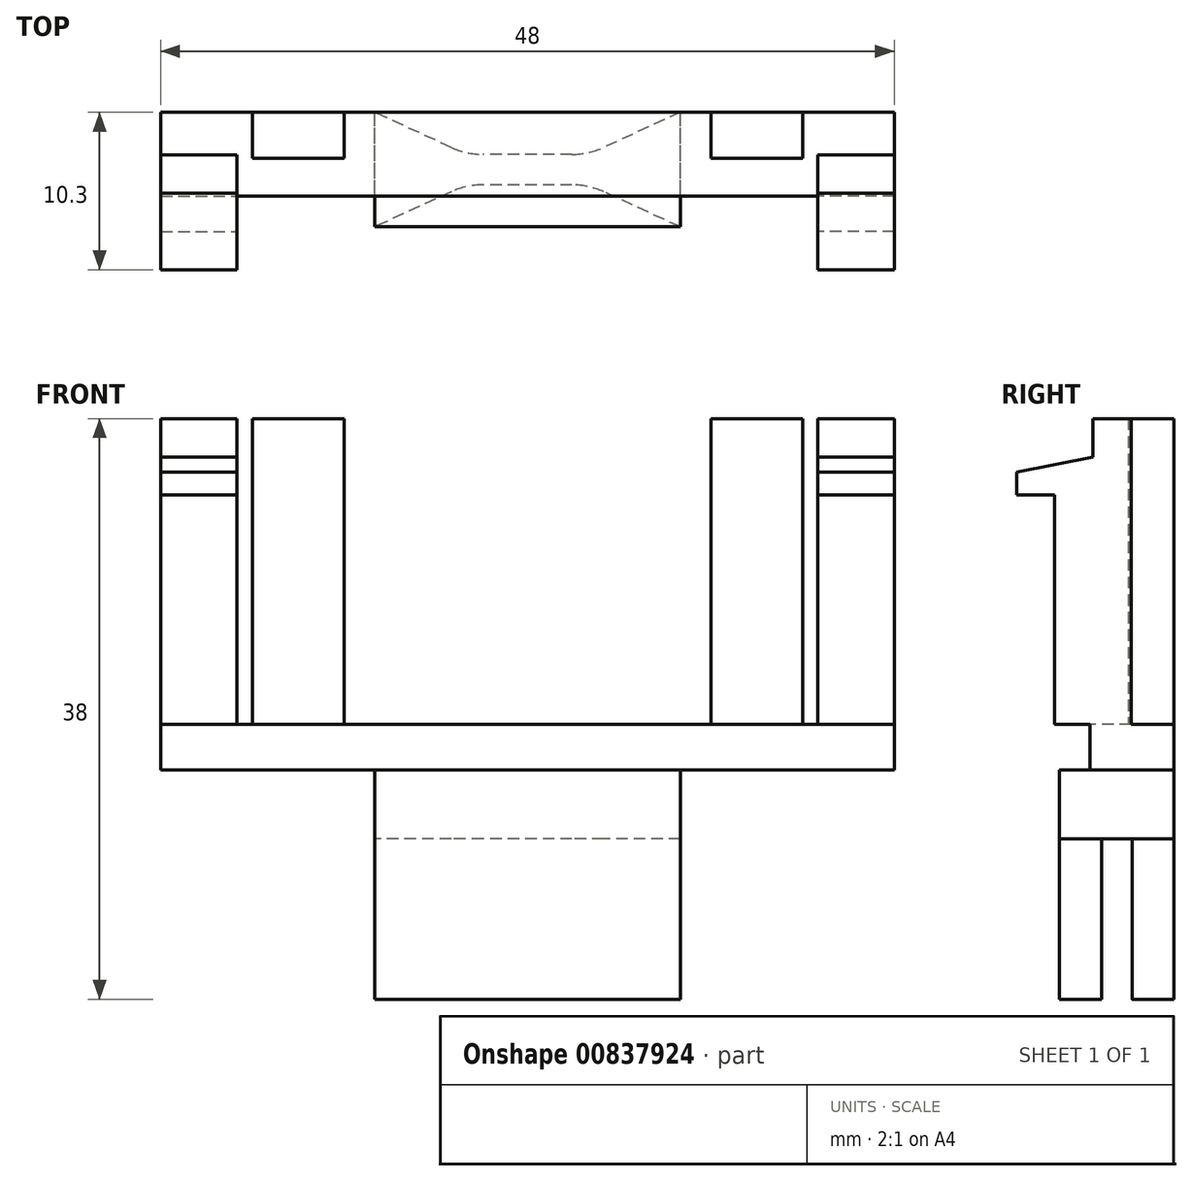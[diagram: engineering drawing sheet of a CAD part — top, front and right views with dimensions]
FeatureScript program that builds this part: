
annotation { "Feature Type Name" : "Feature", "Feature Type Description" : "" }
export const myFeature = defineFeature(function(context is Context, id is Id, definition is map)
    precondition{}
    {
        {
            var Q0;
            Q0=qCreatedBy(makeId("Top.planeOp"),FACE);
            var sketch = newSketch(context, id + "F0", { "sketchPlane" : qUnion([Q0])});
            skLineSegment(sketch, "E0.left", {"start": v(24, -2.75) * mm, "end": v(24, 2.75) * mm});
            skPoint(sketch, "E0.middle", {"position": v(0, 0) * mm});
            skLineSegment(sketch, "E1.bottom", {"start": v(-10, -4.75) * mm, "end": v(10, -4.75) * mm});
            skLineSegment(sketch, "E1.top", {"start": v(-10, 2.75) * mm, "end": v(10, 2.75) * mm});
            skLineSegment(sketch, "E1.left", {"start": v(-10, -4.75) * mm, "end": v(-10, 2.75) * mm});
            skLineSegment(sketch, "E1.right", {"start": v(10, -4.75) * mm, "end": v(10, 2.75) * mm});
            skLineSegment(sketch, "E2", {"start": v(0, -4.75) * mm, "end": v(0, 0) * mm});
            skLineSegment(sketch, "E3", {"start": v(24, 2.75) * mm, "end": v(10, 2.75) * mm});
            skLineSegment(sketch, "E4", {"start": v(24, -2.75) * mm, "end": v(10, -2.75) * mm});
            skLineSegment(sketch, "E5", {"start": v(10, -2.75) * mm, "end": v(-10, -2.75) * mm});
            skSolve(sketch);
        }
        {
            var Q0;
            Q0=makeQuery(id+"F0.imprint","IMPRINT",FACE,{"disambiguationData":[TD([[makeQuery(id+"F0.imprint","IMPRINT",EDGE,{"derivedFrom":sQuery(id+"F0.wireOp",EDGE,"E0.bottom")}),-1.0]])]});
            var Q1;
            {var subQ0=sQuery(id+"F0.wireOp",EDGE,"E0.right");Q1=makeQuery(id+"F0.imprint","IMPRINT",FACE,{"disambiguationData":[TD([[makeQuery(id+"F0.imprint","IMPRINT",EDGE,{"derivedFrom":subQ0}),-1.0]])]});}
            var Q2;
            {var subQ0=sQuery(id+"F0.wireOp",EDGE,"E0.left");Q2=makeQuery(id+"F0.imprint","IMPRINT",FACE,{"disambiguationData":[TD([[makeQuery(id+"F0.imprint","IMPRINT",EDGE,{"derivedFrom":subQ0}),1.0]])]});}
            var Q3;
            {var subQ1=sQuery(id+"F0.wireOp",EDGE,"E1.top");Q3=makeQuery(id+"F0.imprint","IMPRINT",FACE,{"disambiguationData":[TD([[makeQuery(id+"F0.imprint","IMPRINT",EDGE,{"derivedFrom":subQ1}),-1.0]])]});}
            extrude(context, id + "F1", {"entities" : qUnion([Q0, Q1, Q2, Q3]), "depth" : 3 * mm, "offsetDistance" : 25 * mm});
        }
        {
            var Q0;
            {var subQ0=sQuery(id+"F0.wireOp",EDGE,"E2");var subQ1=sQuery(id+"F0.wireOp",EDGE,"E0.bottom");var subQ2=makeQuery(id+"F0.imprint","INTERSECT",VERTEX,{"derivedFrom":[subQ1,subQ0]});Q0=makeQuery(id+"F0.imprint","IMPRINT",FACE,{"disambiguationData":[TD([[makeQuery(id+"F0.imprint","IMPRINT",EDGE,{"disambiguationData":[TD([[subQ2,-1.0]])],"derivedFrom":subQ1}),1.0]])]});}
            var Q1;
            {var subQ0=sQuery(id+"F0.wireOp",EDGE,"E1.right");var subQ1=sQuery(id+"F0.wireOp",EDGE,"E0.bottom");var subQ2=makeQuery(id+"F0.imprint","INTERSECT",VERTEX,{"derivedFrom":[subQ1,subQ0]});Q1=makeQuery(id+"F0.imprint","IMPRINT",FACE,{"disambiguationData":[TD([[makeQuery(id+"F0.imprint","IMPRINT",EDGE,{"disambiguationData":[TD([[subQ2,-1.0]])],"derivedFrom":subQ1}),1.0]])]});}
            var Q2;
            {var subQ0=sQuery(id+"F0.wireOp",EDGE,"E1.top");Q2=makeQuery(id+"F0.imprint","IMPRINT",FACE,{"disambiguationData":[TD([[makeQuery(id+"F0.imprint","IMPRINT",EDGE,{"derivedFrom":subQ0}),-1.0]])]});}
            var Q3;
            {var subQ0=sQuery(id+"F0.wireOp",EDGE,"E1.left");var subQ1=sQuery(id+"F0.wireOp",EDGE,"E1.bottom");var subQ2=makeQuery(id+"F0.imprint","INTERSECT",VERTEX,{"derivedFrom":[subQ1,subQ0]});Q3=makeQuery(id+"F0.imprint","IMPRINT",FACE,{"disambiguationData":[TD([[makeQuery(id+"F0.imprint","IMPRINT",EDGE,{"disambiguationData":[TD([[subQ2,-1.0]])],"derivedFrom":subQ1}),1.0]])]});}
            var Q4;
            {var subQ0=sQuery(id+"F0.wireOp",EDGE,"E1.right");var subQ1=sQuery(id+"F0.wireOp",EDGE,"E1.bottom");var subQ2=makeQuery(id+"F0.imprint","INTERSECT",VERTEX,{"derivedFrom":[subQ1,subQ0]});Q4=makeQuery(id+"F0.imprint","IMPRINT",FACE,{"disambiguationData":[TD([[makeQuery(id+"F0.imprint","IMPRINT",EDGE,{"disambiguationData":[TD([[subQ2,1.0]])],"derivedFrom":subQ1}),1.0]])]});}
            var Q5;
            Q5=sQuery(id+"F0.wireOp",EDGE,"E1.bottom");
            extrude(context, id + "F2", {"entities" : qUnion([Q0, Q1, Q2, Q3, Q4]), "operationType" : NewBodyOperationType.ADD, "surfaceEntities" : qUnion([Q5]), "oppositeDirection" : true, "depth" : 4.5 * mm, "offsetDistance" : 25 * mm});
        }
        {
            var Q0;
            Q0=makeQuery(id+"F2.opExtrude","CAP_FACE",FACE,{"disambiguationData":[OSD([sQuery(id+"F0.wireOp",EDGE,"E1.bottom"),sQuery(id+"F0.wireOp",EDGE,"E1.top"),sQuery(id+"F0.wireOp",EDGE,"E1.left"),sQuery(id+"F0.wireOp",EDGE,"E1.right")])],"isStart":false});
            var sketch = newSketch(context, id + "F3", { "sketchPlane" : qUnion([Q0])});
            skLineSegment(sketch, "E6", {"start": v(10, -2.75) * mm, "end": v(4, 0) * mm});
            skLineSegment(sketch, "E7", {"start": v(4, 0) * mm, "end": v(-4, 0) * mm});
            skLineSegment(sketch, "E8", {"start": v(-4, 0) * mm, "end": v(-10, -2.75) * mm});
            skLineSegment(sketch, "E9", {"start": v(0, -2.75) * mm, "end": v(0, 4.75) * mm});
            skLineSegment(sketch, "E10", {"start": v(10, 1) * mm, "end": v(-10, 1) * mm});
            skLineSegment(sketch, "E11.MirrorCS", {"start": v(10, 4.75) * mm, "end": v(4, 2) * mm});
            skLineSegment(sketch, "E12.MirrorCS", {"start": v(4, 2) * mm, "end": v(-4, 2) * mm});
            skLineSegment(sketch, "E13.MirrorCS", {"start": v(-4, 2) * mm, "end": v(-10, 4.75) * mm});
            skSolve(sketch);
        }
        {
            var Q0;
            {var subQ0=sQuery(id+"F3.wireOp",EDGE,"E6");Q0=makeQuery(id+"F3.imprint","IMPRINT",FACE,{"disambiguationData":[TD([[makeQuery(id+"F3.imprint","IMPRINT",EDGE,{"derivedFrom":subQ0}),1.0]])]});}
            var Q1;
            {var subQ0=sQuery(id+"F3.wireOp",EDGE,"E8");Q1=makeQuery(id+"F3.imprint","IMPRINT",FACE,{"disambiguationData":[TD([[makeQuery(id+"F3.imprint","IMPRINT",EDGE,{"derivedFrom":subQ0}),1.0]])]});}
            var Q2;
            {var subQ5=sQuery(id+"F3.wireOp",EDGE,"E11.MirrorCS");Q2=makeQuery(id+"F3.imprint","IMPRINT",FACE,{"disambiguationData":[TD([[makeQuery(id+"F3.imprint","IMPRINT",EDGE,{"derivedFrom":subQ5}),-1.0]])]});}
            var Q3;
            {var subQ5=sQuery(id+"F3.wireOp",EDGE,"E13.MirrorCS");Q3=makeQuery(id+"F3.imprint","IMPRINT",FACE,{"disambiguationData":[TD([[makeQuery(id+"F3.imprint","IMPRINT",EDGE,{"derivedFrom":subQ5}),-1.0]])]});}
            extrude(context, id + "F4", {"entities" : qUnion([Q0, Q1, Q2, Q3]), "operationType" : NewBodyOperationType.ADD, "depth" : 10.5 * mm, "offsetDistance" : 25 * mm});
        }
        {
            var Q0;
            Q0=makeQuery(id+"F1.opExtrude","CAP_FACE",FACE,{"disambiguationData":[OSD([sQuery(id+"F0.wireOp",EDGE,"E0.bottom"),sQuery(id+"F0.wireOp",EDGE,"E0.top"),sQuery(id+"F0.wireOp",EDGE,"E0.left"),sQuery(id+"F0.wireOp",EDGE,"E0.right"),sQuery(id+"F0.wireOp",EDGE,"E1.top")])],"isStart":false});
            var sketch = newSketch(context, id + "F5", { "sketchPlane" : qUnion([Q0])});
            skLineSegment(sketch, "E14.bottom", {"start": v(12, 2.75) * mm, "end": v(18, 2.75) * mm});
            skLineSegment(sketch, "E14.top", {"start": v(12, -0.25) * mm, "end": v(18, -0.25) * mm});
            skLineSegment(sketch, "E14.left", {"start": v(12, 2.75) * mm, "end": v(12, -0.25) * mm});
            skLineSegment(sketch, "E14.right", {"start": v(18, 2.75) * mm, "end": v(18, -0.25) * mm});
            skLineSegment(sketch, "E15.bottom", {"start": v(24, -0.05) * mm, "end": v(19, -0.05) * mm});
            skLineSegment(sketch, "E15.top", {"start": v(24, -5.05) * mm, "end": v(19, -5.05) * mm});
            skLineSegment(sketch, "E15.left", {"start": v(24, -0.05) * mm, "end": v(24, -5.05) * mm});
            skLineSegment(sketch, "E15.right", {"start": v(19, -0.05) * mm, "end": v(19, -5.05) * mm});
            skSolve(sketch);
        }
        {
            var Q0;
            Q0=makeQuery(id+"F5.imprint","IMPRINT",FACE,{"disambiguationData":[TD([[makeQuery(id+"F5.imprint","IMPRINT",EDGE,{"derivedFrom":sQuery(id+"F5.wireOp",EDGE,"E14.bottom")}),-1.0]])]});
            var Q1;
            {var subQ0=sQuery(id+"F5.wireOp",EDGE,"E15.bottom");Q1=makeQuery(id+"F5.imprint","IMPRINT",FACE,{"disambiguationData":[TD([[makeQuery(id+"F5.imprint","IMPRINT",EDGE,{"derivedFrom":subQ0}),1.0]])]});}
            var Q2;
            {var subQ0=sQuery(id+"F5.wireOp",EDGE,"E15.top");Q2=makeQuery(id+"F5.imprint","IMPRINT",FACE,{"disambiguationData":[TD([[makeQuery(id+"F5.imprint","IMPRINT",EDGE,{"derivedFrom":subQ0}),-1.0]])]});}
            var Q3;
            Q3=makeQuery(id+"F5.imprint","IMPRINT",FACE,{"disambiguationData":[TD([[makeQuery(id+"F5.imprint","IMPRINT",EDGE,{"derivedFrom":sQuery(id+"F5.wireOp",EDGE,"5ea3a386-2e72-4d6f-82df-83e3c4ea288f0.MirrorCS")}),-1.0]])]});
            var Q4;
            {var subQ0=sQuery(id+"F5.wireOp",EDGE,"6e2690fa-45c8-4787-880a-55a10225b8a60.MirrorCS");Q4=makeQuery(id+"F5.imprint","IMPRINT",FACE,{"disambiguationData":[TD([[makeQuery(id+"F5.imprint","IMPRINT",EDGE,{"derivedFrom":subQ0}),-1.0]])]});}
            var Q5;
            {var subQ0=sQuery(id+"F5.wireOp",EDGE,"0a7195a1-aad8-4bab-bf7f-33c16b91a9020.MirrorCS");Q5=makeQuery(id+"F5.imprint","IMPRINT",FACE,{"disambiguationData":[TD([[makeQuery(id+"F5.imprint","IMPRINT",EDGE,{"derivedFrom":subQ0}),1.0]])]});}
            var Q6;
            Q6=makeQuery(id+"F5.imprint","IMPRINT",FACE,{"disambiguationData":[TD([[makeQuery(id+"F5.imprint","IMPRINT",EDGE,{"derivedFrom":sQuery(id+"F5.wireOp",EDGE,"E14.bottom")}),1.0]])]});
            extrude(context, id + "F6", {"entities" : qUnion([Q0, Q1, Q2, Q3, Q4, Q5, Q6]), "operationType" : NewBodyOperationType.ADD, "depth" : 15 * mm, "offsetDistance" : 25 * mm});
        }
        {
            var Q0;
            Q0=makeQuery(id+"F6.opExtrude","CAP_FACE",FACE,{"disambiguationData":[OSD([sQuery(id+"F5.wireOp",EDGE,"E15.bottom"),sQuery(id+"F5.wireOp",EDGE,"E15.top"),sQuery(id+"F5.wireOp",EDGE,"E15.left"),sQuery(id+"F5.wireOp",EDGE,"E15.right")])],"isStart":false});
            var sketch = newSketch(context, id + "F7", { "sketchPlane" : qUnion([Q0])});
            skLineSegment(sketch, "E16.bottom", {"start": v(19, -0.05) * mm, "end": v(24, -0.05) * mm});
            skLineSegment(sketch, "E16.top", {"start": v(19, -2.55) * mm, "end": v(24, -2.55) * mm});
            skLineSegment(sketch, "E16.left", {"start": v(19, -0.05) * mm, "end": v(19, -2.55) * mm});
            skLineSegment(sketch, "E16.right", {"start": v(24, -0.05) * mm, "end": v(24, -2.55) * mm});
            skSolve(sketch);
        }
        {
            var Q0;
            Q0=makeQuery(id+"F7.imprint","IMPRINT",FACE,{"disambiguationData":[TD([[makeQuery(id+"F7.imprint","IMPRINT",EDGE,{"derivedFrom":sQuery(id+"F7.wireOp",EDGE,"e6cad59b-8b4a-41b5-838e-72c1b71bfee10.MirrorCS")}),1.0]])]});
            var Q1;
            Q1=makeQuery(id+"F6.opExtrude","CAP_FACE",FACE,{"disambiguationData":[OSD([sQuery(id+"F5.wireOp",EDGE,"5ea3a386-2e72-4d6f-82df-83e3c4ea288f0.MirrorCS"),sQuery(id+"F5.wireOp",EDGE,"cba0519a-8970-4dc6-bb50-976fce54e4630.MirrorCS"),sQuery(id+"F5.wireOp",EDGE,"64ce6bfb-654b-4831-a077-69f9ca763c0d0.MirrorCS"),sQuery(id+"F5.wireOp",EDGE,"2814ab19-4fc1-4c3a-880c-0dd651a3744e0.MirrorCS")])],"isStart":false});
            var Q2;
            Q2=makeQuery(id+"F6.opExtrude","CAP_FACE",FACE,{"disambiguationData":[OSD([sQuery(id+"F5.wireOp",EDGE,"E14.bottom"),sQuery(id+"F5.wireOp",EDGE,"E14.top"),sQuery(id+"F5.wireOp",EDGE,"E14.left"),sQuery(id+"F5.wireOp",EDGE,"E14.right")])],"isStart":false});
            var Q3;
            Q3=makeQuery(id+"F7.imprint","IMPRINT",FACE,{"disambiguationData":[TD([[makeQuery(id+"F7.imprint","IMPRINT",EDGE,{"derivedFrom":sQuery(id+"F7.wireOp",EDGE,"E16.bottom")}),1.0]])]});
            extrude(context, id + "F8", {"entities" : qUnion([Q0, Q1, Q2, Q3]), "operationType" : NewBodyOperationType.ADD, "depth" : 5 * mm, "offsetDistance" : 25 * mm});
        }
        {
            var Q0;
            Q0=makeQuery(id+"F8.boolean.opBoolean","MERGE",FACE,{"derivedFrom":[makeQuery(id+"F6.boolean.opBoolean","MERGE",FACE,{"derivedFrom":[makeQuery(id+"F1.opExtrude","SWEPT_FACE",FACE,{"disambiguationData":[OSD([sQuery(id+"F0.wireOp",EDGE,"E0.left")])]}),makeQuery(id+"F6.opExtrude","SWEPT_FACE",FACE,{"disambiguationData":[OSD([sQuery(id+"F5.wireOp",EDGE,"E15.left")])]})]}),makeQuery(id+"F8.opExtrude","SWEPT_FACE",FACE,{"disambiguationData":[OSD([sQuery(id+"F7.wireOp",EDGE,"E16.right")])]})]});
            var sketch = newSketch(context, id + "F9", { "sketchPlane" : qUnion([Q0])});
            skLineSegment(sketch, "E17.bottom", {"start": v(-2.55, 18) * mm, "end": v(-7.55, 18) * mm});
            skLineSegment(sketch, "E17.top", {"start": v(-2.55, 19.5) * mm, "end": v(-7.55, 19.5) * mm});
            skLineSegment(sketch, "E17.left", {"start": v(-2.55, 18) * mm, "end": v(-2.55, 19.5) * mm});
            skLineSegment(sketch, "E17.right", {"start": v(-7.55, 18) * mm, "end": v(-7.55, 19.5) * mm});
            skLineSegment(sketch, "E18", {"start": v(-7.55, 19.5) * mm, "end": v(-2.55, 20.5) * mm});
            skSolve(sketch);
        }
        {
            var Q0;
            Q0=makeQuery(id+"F9.imprint","IMPRINT",FACE,{"disambiguationData":[TD([[makeQuery(id+"F9.imprint","IMPRINT",EDGE,{"derivedFrom":sQuery(id+"F9.wireOp",EDGE,"E17.top")}),1.0]])]});
            var Q1;
            {var subQ0=sQuery(id+"F9.wireOp",EDGE,"E17.top");Q1=makeQuery(id+"F9.imprint","IMPRINT",FACE,{"disambiguationData":[TD([[makeQuery(id+"F9.imprint","IMPRINT",EDGE,{"derivedFrom":subQ0}),-1.0]])]});}
            extrude(context, id + "F10", {"entities" : qUnion([Q0, Q1]), "operationType" : NewBodyOperationType.ADD, "oppositeDirection" : true, "depth" : 5 * mm, "offsetDistance" : 25 * mm});
        }
        {
            var Q0;
            Q0=makeQuery(id+"F1.opExtrude","SWEPT_BODY",BODY,{"disambiguationData":[OSD([sQuery(id+"F0.wireOp",EDGE,"E0.left"),sQuery(id+"F0.wireOp",EDGE,"E1.bottom"),sQuery(id+"F0.wireOp",EDGE,"E1.top"),sQuery(id+"F0.wireOp",EDGE,"E1.left"),sQuery(id+"F0.wireOp",EDGE,"E1.right"),sQuery(id+"F0.wireOp",EDGE,"E3"),sQuery(id+"F0.wireOp",EDGE,"E4")])]});
            var Q1;
            Q1=qCreatedBy(makeId("Right.planeOp"),FACE);
            mirror(context, id + "F11", {"operationType" : NewBodyOperationType.ADD, "entities" : qUnion([Q0]), "mirrorPlane" : qUnion([Q1])});
        }
        {
            var Q0;
            Q0=makeQuery(id+"F4.opExtrude","SWEPT_EDGE",EDGE,{"disambiguationData":[OSD([sQuery(id+"F3.wireOp",EDGE,"E12.MirrorCS"),sQuery(id+"F3.wireOp",EDGE,"E13.MirrorCS")])]});
            var Q1;
            Q1=makeQuery(id+"F4.opExtrude","SWEPT_EDGE",EDGE,{"disambiguationData":[OSD([sQuery(id+"F3.wireOp",EDGE,"E11.MirrorCS"),sQuery(id+"F3.wireOp",EDGE,"E12.MirrorCS")])]});
            var Q2;
            Q2=makeQuery(id+"F4.opExtrude","SWEPT_EDGE",EDGE,{"disambiguationData":[OSD([sQuery(id+"F3.wireOp",EDGE,"E6"),sQuery(id+"F3.wireOp",EDGE,"E7")])]});
            var Q3;
            Q3=makeQuery(id+"F4.opExtrude","SWEPT_EDGE",EDGE,{"disambiguationData":[OSD([sQuery(id+"F3.wireOp",EDGE,"E7"),sQuery(id+"F3.wireOp",EDGE,"E8")])]});
            fillet(context, id + "F12", {"entities" : qUnion([Q0, Q1, Q2, Q3]), "radius" : 5 * mm, "tangentPropagation" : true, "allowEdgeOverflow" : false});
        }
    });
